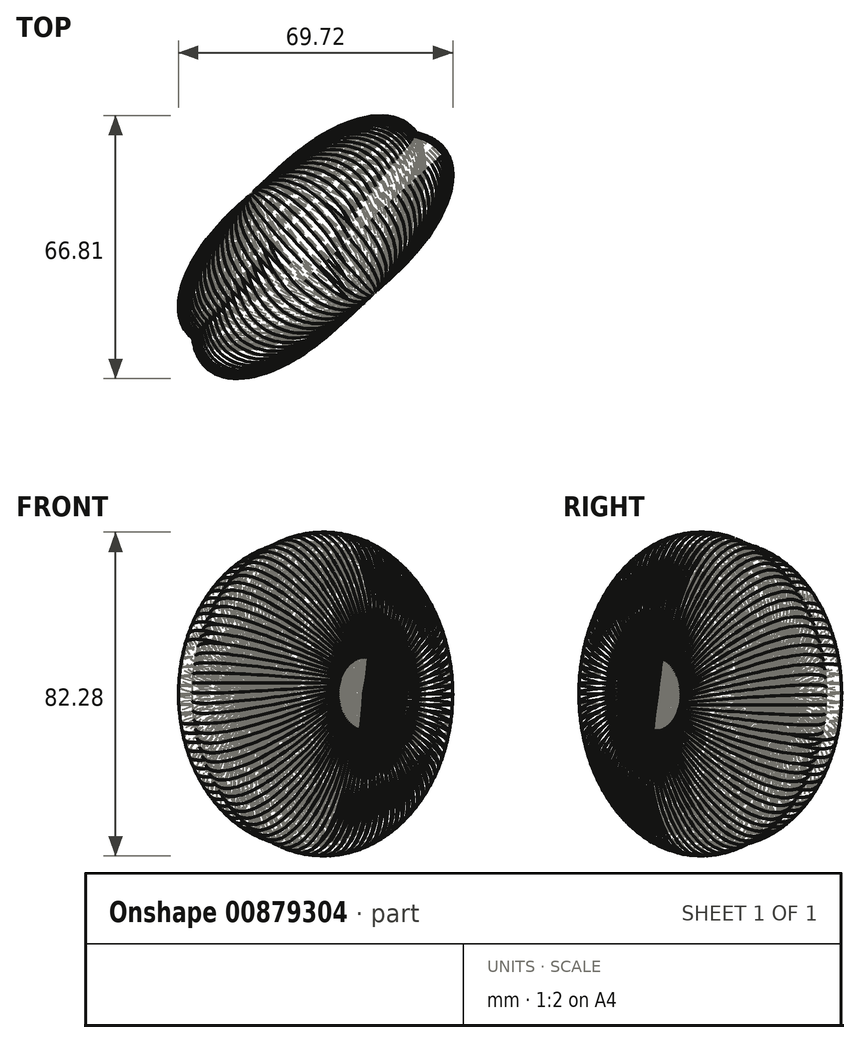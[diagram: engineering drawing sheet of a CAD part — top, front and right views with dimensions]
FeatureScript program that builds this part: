
annotation { "Feature Type Name" : "Feature", "Feature Type Description" : "" }
export const myFeature = defineFeature(function(context is Context, id is Id, definition is map)
    precondition{}
    {
        {
            var Q0;
            Q0=qCreatedBy(makeId("Top.planeOp"),FACE);
            var sketch = newSketch(context, id + "F0", { "sketchPlane" : qUnion([Q0])});
            skEllipse(sketch, "E0", {"center": v(0, 0) * mm, "majorRadius": 40.15 * mm, "minorRadius": 19.3 * mm, "majorAxis": v(0.82, 0.57)});
            skSolve(sketch);
        }
        {
            var Q0;
            Q0=makeQuery(id+"F0.imprint","IMPRINT",FACE,{"disambiguationData":[TD([[makeQuery(id+"F0.imprint","IMPRINT",EDGE,{"derivedFrom":sQuery(id+"F0.wireOp",EDGE,"E0")}),1.0]])]});
            extrude(context, id + "F1", {"entities" : qUnion([Q0]), "depth" : 2.8 * mm, "offsetDistance" : 25 * mm});
        }
        {
            var Q0;
            Q0=makeQuery(id+"F1.opExtrude","CAP_FACE",FACE,{"disambiguationData":[OSD([sQuery(id+"F0.wireOp",EDGE,"E0")])],"isStart":false});
            var sketch = newSketch(context, id + "F2", { "sketchPlane" : qUnion([Q0])});
            skLineSegment(sketch, "E1", {"start": v(-14.13, 13.59) * mm, "end": v(12.2, -15.02) * mm});
            skSolve(sketch);
        }
        {
            var Q0;
            Q0=makeQuery(id+"F1.opExtrude","SWEPT_BODY",BODY,{"disambiguationData":[OSD([sQuery(id+"F0.wireOp",EDGE,"E0")])]});
            var Q1;
            Q1=sQuery(id+"F2.wireOp",EDGE,"E1");
            circularPattern(context, id + "F3", {"entities" : qUnion([Q0]), "axis" : qUnion([Q1]), "angle" : 360 * degree, "instanceCount" : 100, "equalSpace" : true, "isCentered" : true});
        }
    });
